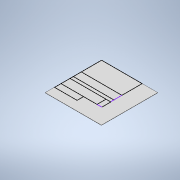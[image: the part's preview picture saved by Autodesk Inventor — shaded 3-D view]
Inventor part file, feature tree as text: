
AUTODESK INVENTOR PART (.ipt)
format: ipt  version: 2022 (Build 260153000, 153)  size: 112,640 bytes
history: native  units: mm
features: sketch x2, other x1, extrude x1
ambient origin geometry x8: Origin, YZ Plane, XZ Plane, XY Plane, X Axis, Y Axis, Z Axis, Center Point
bodies: Body1 (feature_tree)
feature tree (4):
  other  "ソリッド1"
  extrude  "押し出し1"  Depth=500.0mm
  sketch  "スケッチ2"
  sketch  "スケッチ1"
